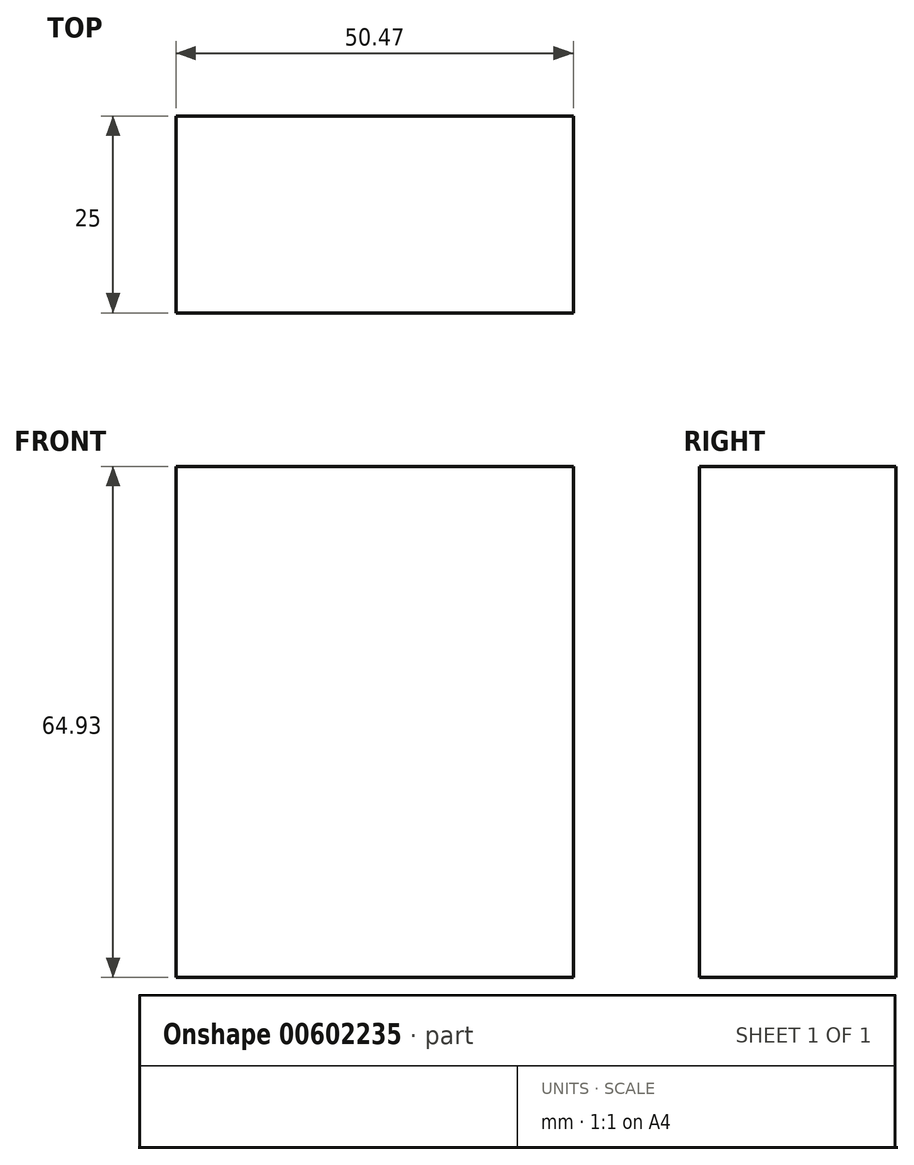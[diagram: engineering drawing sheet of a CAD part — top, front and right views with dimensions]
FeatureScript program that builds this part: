
annotation { "Feature Type Name" : "Feature", "Feature Type Description" : "" }
export const myFeature = defineFeature(function(context is Context, id is Id, definition is map)
    precondition{}
    {
        {
            var Q0;
            Q0=qCreatedBy(makeId("Front.planeOp"),FACE);
            var sketch = newSketch(context, id + "F0", { "sketchPlane" : qUnion([Q0])});
            skLineSegment(sketch, "E0", {"start": v(-36.46, 38.7) * mm, "end": v(-36.46, -26.23) * mm});
            skLineSegment(sketch, "E1", {"start": v(-36.46, 38.7) * mm, "end": v(14, 38.7) * mm});
            skLineSegment(sketch, "E2", {"start": v(-36.46, -26.23) * mm, "end": v(16.68, -26.23) * mm});
            skLineSegment(sketch, "E3", {"start": v(14, 38.7) * mm, "end": v(14, -26.23) * mm});
            skSolve(sketch);
        }
        {
            var Q0;
            {var subQ0=sQuery(id+"F0.wireOp",EDGE,"E0");Q0=makeQuery(id+"F0.imprint","IMPRINT",FACE,{"disambiguationData":[TD([[makeQuery(id+"F0.imprint","IMPRINT",EDGE,{"derivedFrom":subQ0}),1.0]])]});}
            extrude(context, id + "F1", {"entities" : qUnion([Q0]), "depth" : 25 * mm, "offsetDistance" : 25 * mm});
        }
    });
